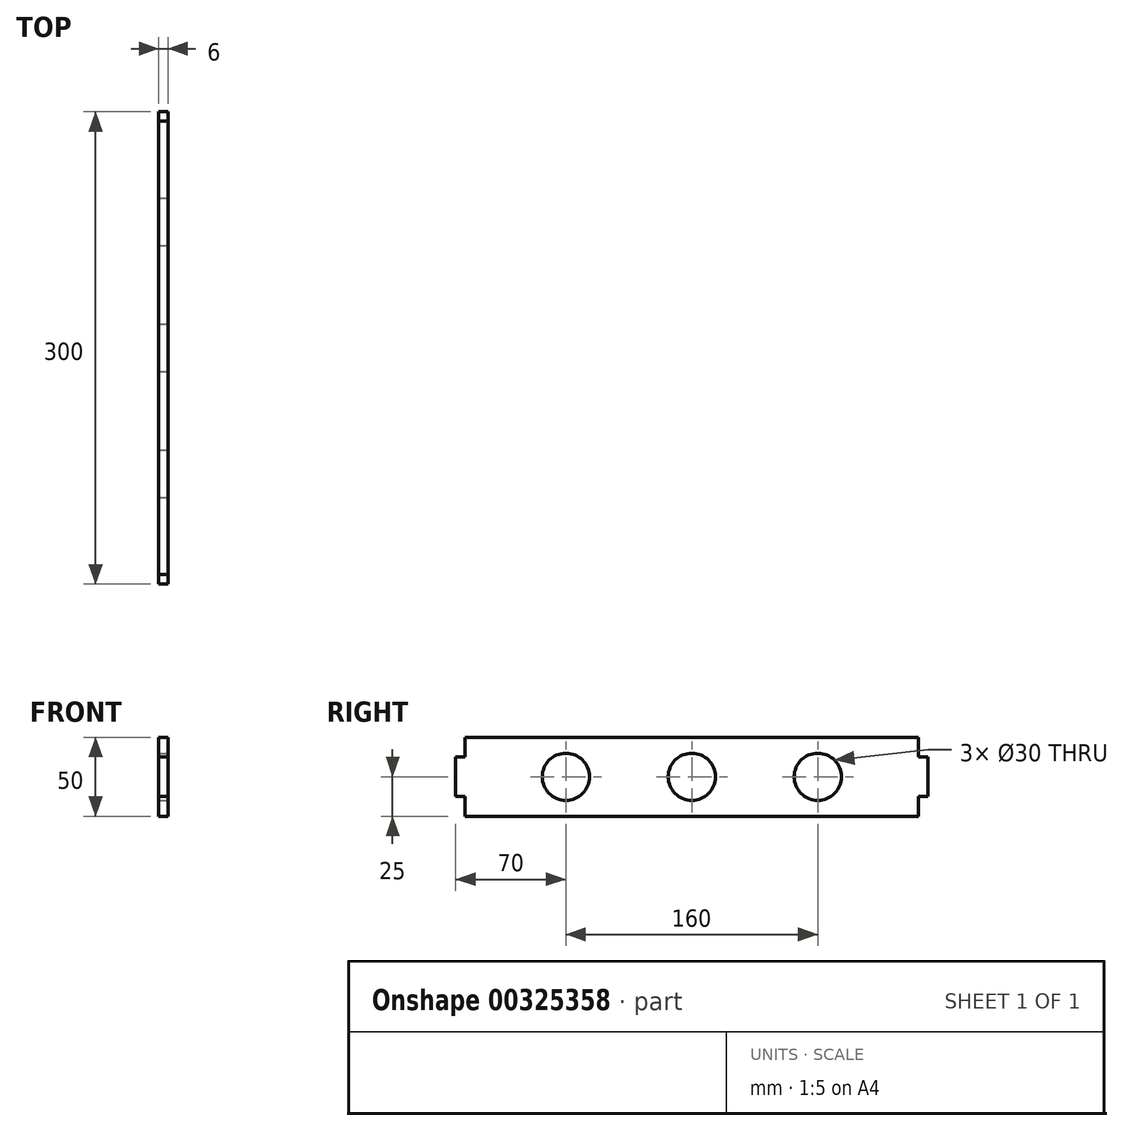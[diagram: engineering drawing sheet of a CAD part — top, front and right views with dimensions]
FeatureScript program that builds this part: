
annotation { "Feature Type Name" : "Feature", "Feature Type Description" : "" }
export const myFeature = defineFeature(function(context is Context, id is Id, definition is map)
    precondition{}
    {
        {
            var Q0;
            Q0=qCreatedBy(makeId("Right.planeOp"),FACE);
            var sketch = newSketch(context, id + "F0", { "sketchPlane" : qUnion([Q0])});
            skLineSegment(sketch, "E0.bottom", {"start": v(-144, 25) * mm, "end": v(144, 25) * mm});
            skLineSegment(sketch, "E0.top", {"start": v(-144, -25) * mm, "end": v(144, -25) * mm});
            skLineSegment(sketch, "E0.left", {"start": v(-144, 25) * mm, "end": v(-144, -25) * mm});
            skLineSegment(sketch, "E0.right", {"start": v(144, 25) * mm, "end": v(144, -25) * mm});
            skPoint(sketch, "E0.middle", {"position": v(0, 0) * mm});
            skLineSegment(sketch, "E1.bottom", {"start": v(-75, 25) * mm, "end": v(75, 25) * mm});
            skLineSegment(sketch, "E1.top", {"start": v(-75, 19) * mm, "end": v(75, 19) * mm});
            skLineSegment(sketch, "E1.left", {"start": v(-75, 25) * mm, "end": v(-75, 19) * mm});
            skLineSegment(sketch, "E1.right", {"start": v(75, 25) * mm, "end": v(75, 19) * mm});
            skPoint(sketch, "E1.middle", {"position": v(0, 22) * mm});
            skLineSegment(sketch, "E2.bottom", {"start": v(-144, 12.5) * mm, "end": v(-138, 12.5) * mm});
            skLineSegment(sketch, "E2.top", {"start": v(-144, -12.5) * mm, "end": v(-138, -12.5) * mm});
            skLineSegment(sketch, "E2.left", {"start": v(-144, 12.5) * mm, "end": v(-144, -12.5) * mm});
            skLineSegment(sketch, "E2.right", {"start": v(-138, 12.5) * mm, "end": v(-138, -12.5) * mm});
            skPoint(sketch, "E2.middle", {"position": v(-141, 0) * mm});
            skLineSegment(sketch, "E3.bottom", {"start": v(144, 12.5) * mm, "end": v(138, 12.5) * mm});
            skLineSegment(sketch, "E3.top", {"start": v(144, -12.5) * mm, "end": v(138, -12.5) * mm});
            skLineSegment(sketch, "E3.left", {"start": v(144, 12.5) * mm, "end": v(144, -12.5) * mm});
            skLineSegment(sketch, "E3.right", {"start": v(138, 12.5) * mm, "end": v(138, -12.5) * mm});
            skPoint(sketch, "E3.middle", {"position": v(141, 0) * mm});
            skPoint(sketch, "E3.middle.positionSnap0", {"position": v(144, 0) * mm});
            skPoint(sketch, "E3.centerSnap0", {"position": v(144, 0) * mm});
            skLineSegment(sketch, "E4.bottom", {"start": v(-75, -25) * mm, "end": v(75, -25) * mm});
            skLineSegment(sketch, "E4.top", {"start": v(-75, -19) * mm, "end": v(75, -19) * mm});
            skLineSegment(sketch, "E4.left", {"start": v(-75, -25) * mm, "end": v(-75, -19) * mm});
            skLineSegment(sketch, "E4.right", {"start": v(75, -25) * mm, "end": v(75, -19) * mm});
            skPoint(sketch, "E4.middle", {"position": v(0, -22) * mm});
            skLineSegment(sketch, "E5.top", {"start": v(-75, 31) * mm, "end": v(75, 31) * mm});
            skLineSegment(sketch, "E5.left", {"start": v(-75, 25) * mm, "end": v(-75, 31) * mm});
            skLineSegment(sketch, "E5.right", {"start": v(75, 25) * mm, "end": v(75, 31) * mm});
            skLineSegment(sketch, "E6.top", {"start": v(-75, -31) * mm, "end": v(75, -31) * mm});
            skLineSegment(sketch, "E6.left", {"start": v(-75, -25) * mm, "end": v(-75, -31) * mm});
            skLineSegment(sketch, "E6.right", {"start": v(75, -25) * mm, "end": v(75, -31) * mm});
            skLineSegment(sketch, "E7.bottom", {"start": v(-144, 12.5) * mm, "end": v(-150, 12.5) * mm});
            skLineSegment(sketch, "E7.top", {"start": v(-144, -12.5) * mm, "end": v(-150, -12.5) * mm});
            skLineSegment(sketch, "E7.right", {"start": v(-150, 12.5) * mm, "end": v(-150, -12.5) * mm});
            skLineSegment(sketch, "E8.bottom", {"start": v(144, 12.5) * mm, "end": v(150, 12.5) * mm});
            skLineSegment(sketch, "E8.top", {"start": v(144, -12.5) * mm, "end": v(150, -12.5) * mm});
            skLineSegment(sketch, "E8.right", {"start": v(150, 12.5) * mm, "end": v(150, -12.5) * mm});
            skSolve(sketch);
        }
        {
            var Q0;
            Q0=makeQuery(id+"F0.imprint","IMPRINT",FACE,{"disambiguationData":[TD([[makeQuery(id+"F0.imprint","IMPRINT",EDGE,{"derivedFrom":sQuery(id+"F0.wireOp",EDGE,"E1.top")}),-1.0]])]});
            var Q1;
            Q1=makeQuery(id+"F0.imprint","IMPRINT",FACE,{"disambiguationData":[TD([[makeQuery(id+"F0.imprint","IMPRINT",EDGE,{"derivedFrom":sQuery(id+"F0.wireOp",EDGE,"E1.top")}),1.0]])]});
            var Q2;
            Q2=makeQuery(id+"F0.imprint","IMPRINT",FACE,{"disambiguationData":[TD([[makeQuery(id+"F0.imprint","IMPRINT",EDGE,{"derivedFrom":sQuery(id+"F0.wireOp",EDGE,"E4.bottom")}),-1.0]])]});
            var Q3;
            Q3=makeQuery(id+"F0.imprint","IMPRINT",FACE,{"disambiguationData":[TD([[makeQuery(id+"F0.imprint","IMPRINT",EDGE,{"derivedFrom":sQuery(id+"F0.wireOp",EDGE,"E4.top")}),-1.0]])]});
            var Q4;
            Q4=makeQuery(id+"F0.imprint","IMPRINT",FACE,{"disambiguationData":[TD([[makeQuery(id+"F0.imprint","IMPRINT",EDGE,{"derivedFrom":sQuery(id+"F0.wireOp",EDGE,"E2.bottom")}),-1.0]])]});
            var Q5;
            Q5=makeQuery(id+"F0.imprint","IMPRINT",FACE,{"disambiguationData":[TD([[makeQuery(id+"F0.imprint","IMPRINT",EDGE,{"derivedFrom":sQuery(id+"F0.wireOp",EDGE,"E7.bottom")}),1.0]])]});
            var Q6;
            Q6=makeQuery(id+"F0.imprint","IMPRINT",FACE,{"disambiguationData":[TD([[makeQuery(id+"F0.imprint","IMPRINT",EDGE,{"derivedFrom":sQuery(id+"F0.wireOp",EDGE,"E8.bottom")}),-1.0]])]});
            var Q7;
            Q7=makeQuery(id+"F0.imprint","IMPRINT",FACE,{"disambiguationData":[TD([[makeQuery(id+"F0.imprint","IMPRINT",EDGE,{"derivedFrom":sQuery(id+"F0.wireOp",EDGE,"E3.bottom")}),1.0]])]});
            extrude(context, id + "F1", {"entities" : qUnion([Q0, Q1, Q2, Q3, Q4, Q5, Q6, Q7]), "depth" : 6 * mm});
        }
        {
            var Q0;
            Q0=makeQuery(id+"F1.opExtrude","CAP_FACE",FACE,{"disambiguationData":[OSD([sQuery(id+"F0.wireOp",EDGE,"E0.bottom"),sQuery(id+"F0.wireOp",EDGE,"E0.top"),sQuery(id+"F0.wireOp",EDGE,"E0.left"),sQuery(id+"F0.wireOp",EDGE,"E0.right"),sQuery(id+"F0.wireOp",EDGE,"E1.bottom"),sQuery(id+"F0.wireOp",EDGE,"E6.top"),sQuery(id+"F0.wireOp",EDGE,"E6.left"),sQuery(id+"F0.wireOp",EDGE,"E6.right"),sQuery(id+"F0.wireOp",EDGE,"E7.bottom"),sQuery(id+"F0.wireOp",EDGE,"E7.top"),sQuery(id+"F0.wireOp",EDGE,"E7.right"),sQuery(id+"F0.wireOp",EDGE,"E8.bottom"),sQuery(id+"F0.wireOp",EDGE,"E8.top"),sQuery(id+"F0.wireOp",EDGE,"E8.right")])],"isStart":false});
            var sketch = newSketch(context, id + "F2", { "sketchPlane" : qUnion([Q0])});
            skCircle(sketch, "E9", {"center": v(0, 0) * mm, "radius": 15 * mm});
            skCircle(sketch, "E10", {"center": v(-80, 0) * mm, "radius": 15 * mm});
            skCircle(sketch, "E11", {"center": v(80, 0) * mm, "radius": 15 * mm});
            skSolve(sketch);
        }
        {
            var Q0;
            Q0 = qSketchRegion(id + "F2", true);
            extrude(context, id + "F3", {"entities" : qUnion([Q0]), "operationType" : NewBodyOperationType.REMOVE, "endBound" : BoundingType.UP_TO_NEXT, "oppositeDirection" : true, "depth" : 25 * mm});
        }
    });
